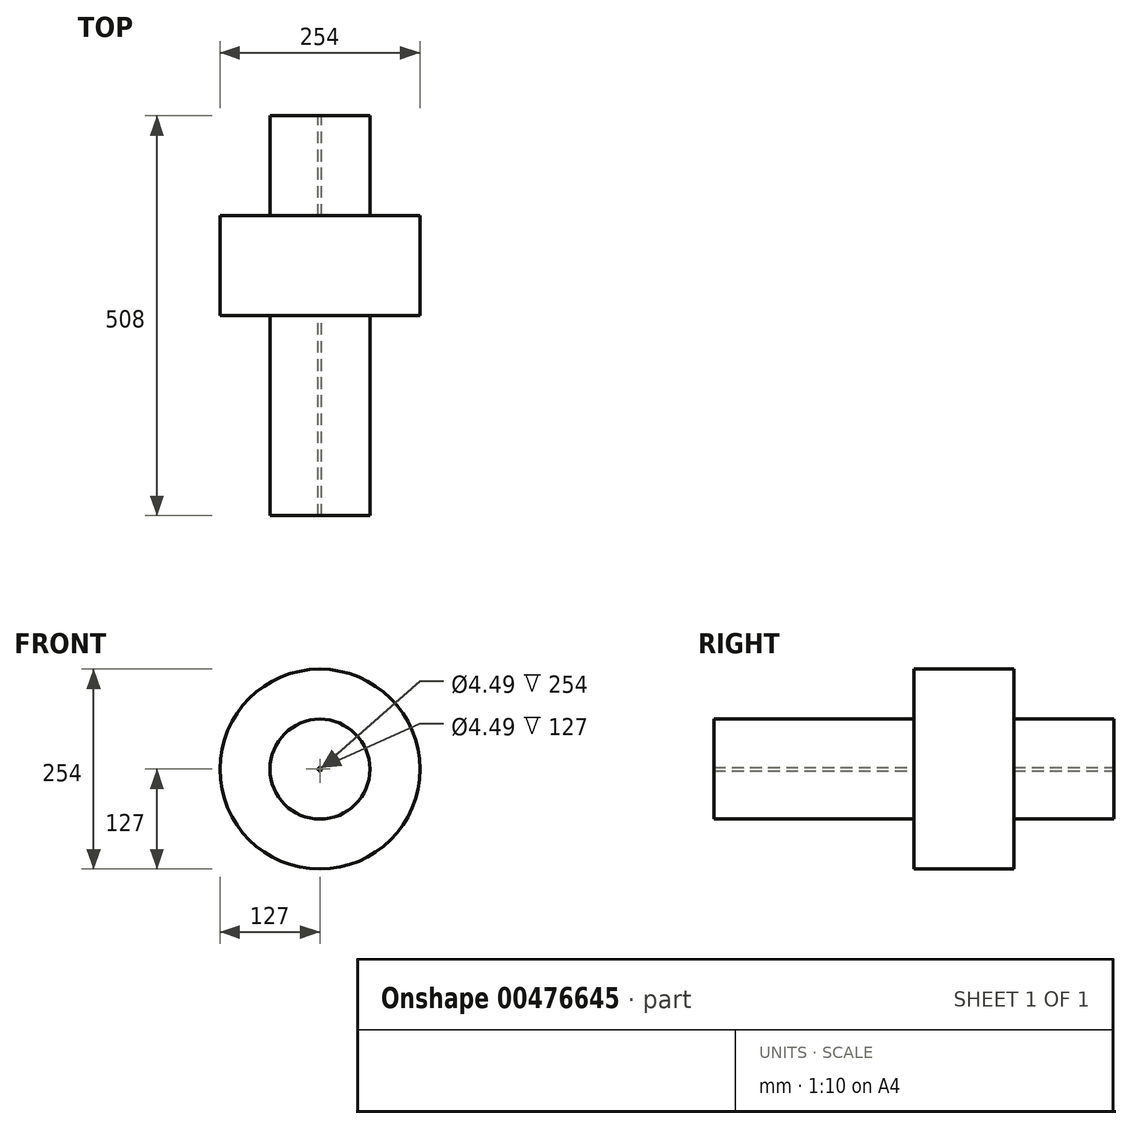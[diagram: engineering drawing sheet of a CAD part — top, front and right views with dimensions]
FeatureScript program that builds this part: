
annotation { "Feature Type Name" : "Feature", "Feature Type Description" : "" }
export const myFeature = defineFeature(function(context is Context, id is Id, definition is map)
    precondition{}
    {
        {
            var Q0;
            Q0=qCreatedBy(makeId("Front.planeOp"),FACE);
            var sketch = newSketch(context, id + "F0", { "sketchPlane" : qUnion([Q0])});
            skCircle(sketch, "E0", {"center": v(0, 0) * mm, "radius": 2.24 * mm});
            skCircle(sketch, "E1", {"center": v(0, 0) * mm, "radius": 63.5 * mm});
            skSolve(sketch);
        }
        {
            var Q0;
            Q0 = qSketchRegion(id + "F0", true);
            extrude(context, id + "F1", {"entities" : qUnion([Q0]), "depth" : 508 * mm});
        }
        {
            var Q0;
            Q0=qCreatedBy(makeId("Front.planeOp"),FACE);
            cPlane(context, id + "F2", {"entities" : qUnion([Q0]), "cplaneType" : CPlaneType.OFFSET, "offset" : 127 * mm, "width" : 152.4 * mm, "height" : 152.4 * mm});
        }
        {
            var Q0;
            Q0=qCreatedBy(id+"F2.planeOp",FACE);
            var sketch = newSketch(context, id + "F3", { "sketchPlane" : qUnion([Q0])});
            skCircle(sketch, "E2.0.0", {"center": v(0, 0) * mm, "radius": 63.5 * mm, "construction": true});
            skCircle(sketch, "E3", {"center": v(0, 0) * mm, "radius": 127 * mm});
            skSolve(sketch);
        }
        {
            var Q0;
            Q0 = qSketchRegion(id + "F3", true);
            extrude(context, id + "F4", {"entities" : qUnion([Q0]), "operationType" : NewBodyOperationType.ADD, "depth" : 127 * mm});
        }
    });
